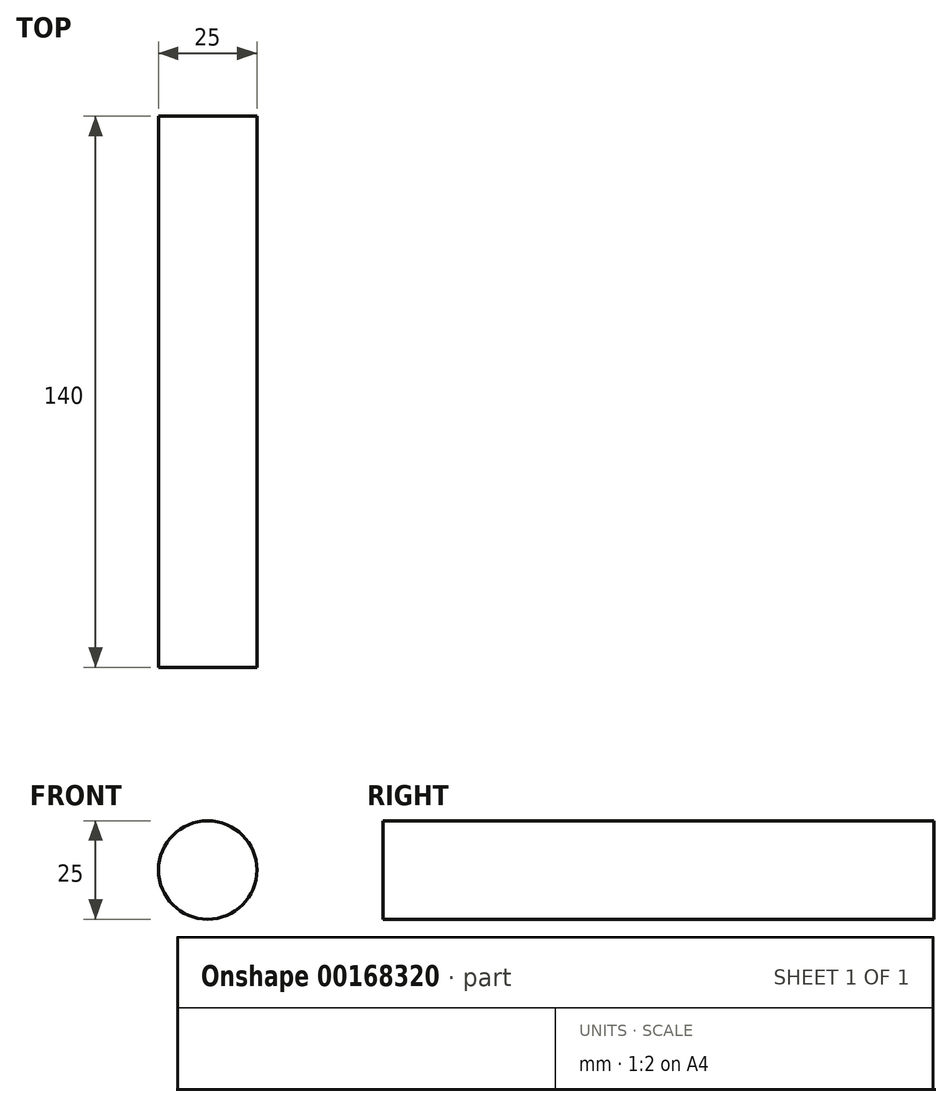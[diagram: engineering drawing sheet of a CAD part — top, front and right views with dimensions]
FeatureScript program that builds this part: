
annotation { "Feature Type Name" : "Feature", "Feature Type Description" : "" }
export const myFeature = defineFeature(function(context is Context, id is Id, definition is map)
    precondition{}
    {
        {
            var Q0;
            Q0=qCreatedBy(makeId("Front.planeOp"),FACE);
            var sketch = newSketch(context, id + "F0", { "sketchPlane" : qUnion([Q0])});
            skCircle(sketch, "E0", {"center": v(0, 0) * mm, "radius": 12.5 * mm});
            skSolve(sketch);
        }
        {
            var Q0;
            Q0 = qSketchRegion(id + "F0", true);
            extrude(context, id + "F1", {"entities" : qUnion([Q0]), "depth" : 70 * mm});
        }
        {
            var Q0;
            Q0 = qSketchRegion(id + "F0", true);
            extrude(context, id + "F2", {"entities" : qUnion([Q0]), "operationType" : NewBodyOperationType.ADD, "oppositeDirection" : true, "depth" : 70 * mm});
        }
    });
